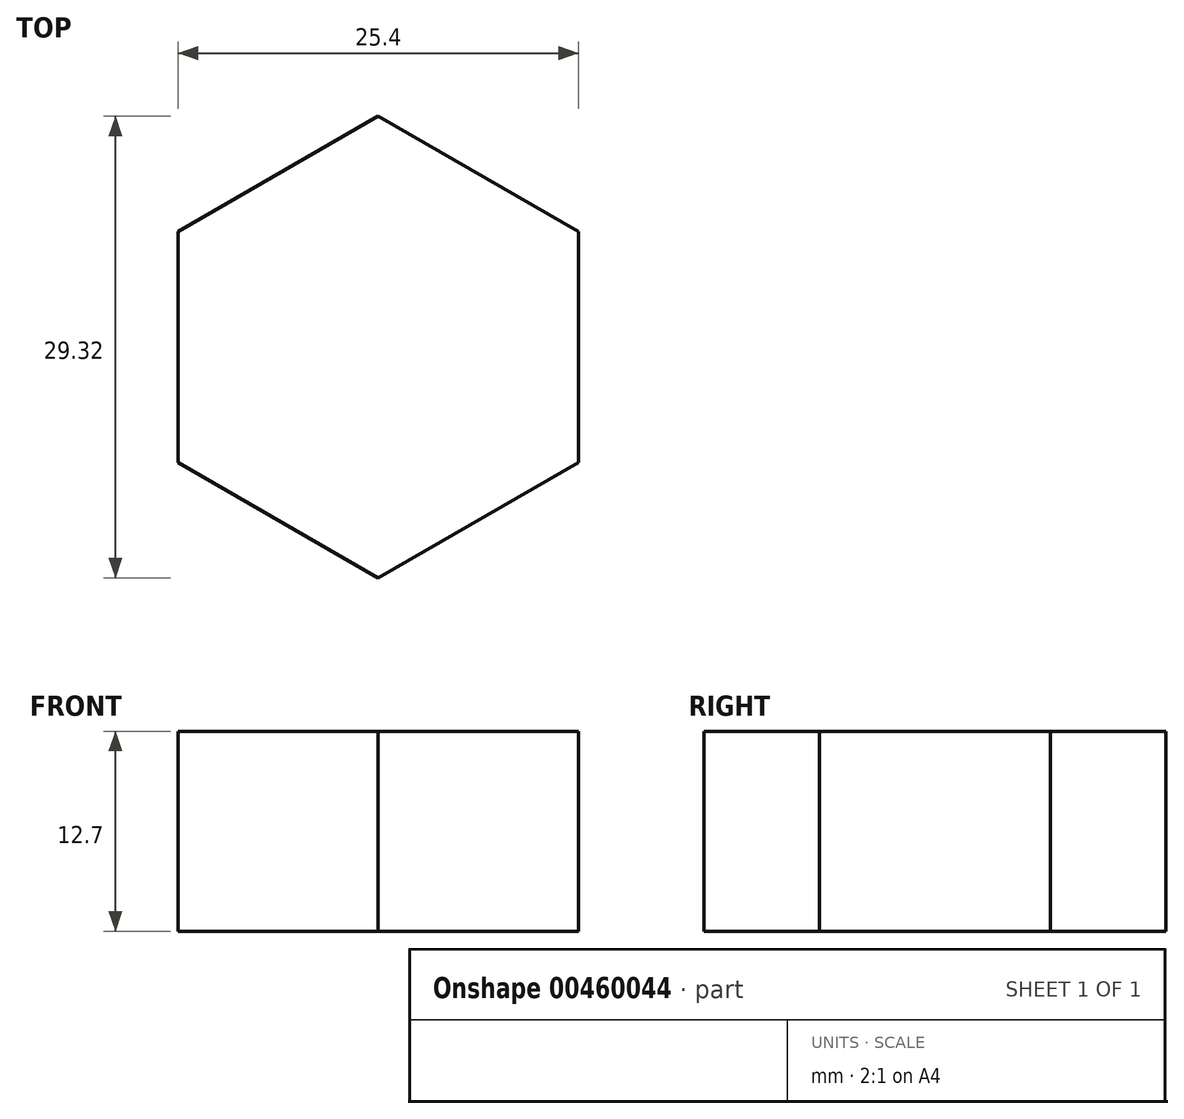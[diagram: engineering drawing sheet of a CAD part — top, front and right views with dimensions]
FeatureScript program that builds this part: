
annotation { "Feature Type Name" : "Feature", "Feature Type Description" : "" }
export const myFeature = defineFeature(function(context is Context, id is Id, definition is map)
    precondition{}
    {
        {
            var Q0;
            Q0=qCreatedBy(makeId("Top.planeOp"),FACE);
            var sketch = newSketch(context, id + "F0", { "sketchPlane" : qUnion([Q0])});
            skCircle(sketch, "E0.cCircle", {"center": v(0, 0) * mm, "radius": 12.7 * mm, "construction": true});
            skLineSegment(sketch, "E0.0", {"start": v(12.7, 7.33) * mm, "end": v(12.7, -7.33) * mm});
            skLineSegment(sketch, "E0.1", {"start": v(12.7, -7.33) * mm, "end": v(0, -14.66) * mm});
            skLineSegment(sketch, "E0.2", {"start": v(0, -14.66) * mm, "end": v(-12.7, -7.33) * mm});
            skLineSegment(sketch, "E0.3", {"start": v(-12.7, -7.33) * mm, "end": v(-12.7, 7.33) * mm});
            skLineSegment(sketch, "E0.4", {"start": v(-12.7, 7.33) * mm, "end": v(0, 14.66) * mm});
            skLineSegment(sketch, "E0.5", {"start": v(0, 14.66) * mm, "end": v(12.7, 7.33) * mm});
            skPoint(sketch, "E0.0.midPoint", {"position": v(12.7, 0) * mm});
            skSolve(sketch);
        }
        {
            var Q0;
            Q0 = qSketchRegion(id + "F0", true);
            extrude(context, id + "F1", {"entities" : qUnion([Q0]), "depth" : 12.7 * mm, "offsetDistance" : 25.4 * mm});
        }
    });
